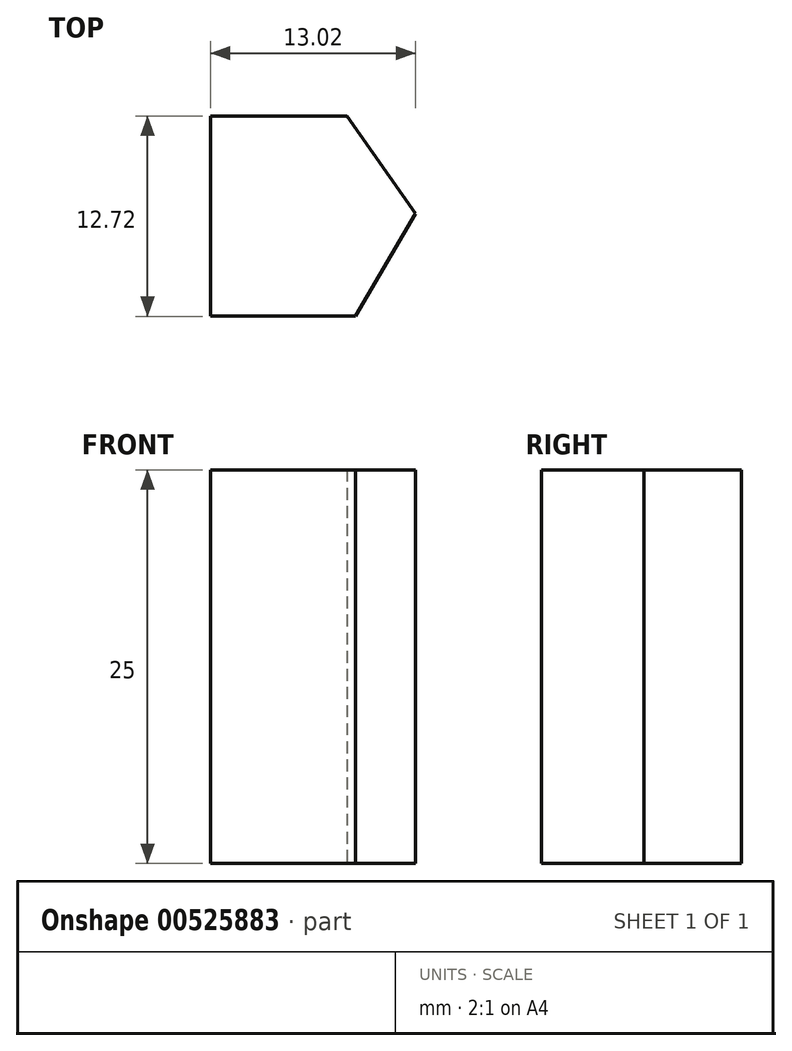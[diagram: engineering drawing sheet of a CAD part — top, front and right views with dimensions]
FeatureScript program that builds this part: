
annotation { "Feature Type Name" : "Feature", "Feature Type Description" : "" }
export const myFeature = defineFeature(function(context is Context, id is Id, definition is map)
    precondition{}
    {
        {
            var Q0;
            Q0=qCreatedBy(makeId("Top.planeOp"),FACE);
            var sketch = newSketch(context, id + "F0", { "sketchPlane" : qUnion([Q0])});
            skLineSegment(sketch, "E0", {"start": v(-57.05, 52.09) * mm, "end": v(-57.05, 26.66) * mm});
            skLineSegment(sketch, "E1", {"start": v(-68.83, 52.09) * mm, "end": v(-44.03, 52.09) * mm});
            skLineSegment(sketch, "E2", {"start": v(-30.38, 52.09) * mm, "end": v(-23.56, 41.55) * mm});
            skLineSegment(sketch, "E3", {"start": v(-17.98, 52.09) * mm, "end": v(-32.86, 26.66) * mm});
            skLineSegment(sketch, "E4", {"start": v(-9.3, 52.09) * mm, "end": v(-9.3, 26.66) * mm});
            skLineSegment(sketch, "E5", {"start": v(-9.3, 26.66) * mm, "end": v(4.96, 26.66) * mm});
            skLineSegment(sketch, "E6", {"start": v(16.74, 52.09) * mm, "end": v(16.74, 26.66) * mm});
            skLineSegment(sketch, "E7", {"start": v(16.74, 26.66) * mm, "end": v(27.28, 26.66) * mm});
            skLineSegment(sketch, "E8", {"start": v(16.74, 39.37) * mm, "end": v(27.28, 39.37) * mm});
            skLineSegment(sketch, "E9", {"start": v(16.74, 52.09) * mm, "end": v(27.28, 52.09) * mm});
            skLineSegment(sketch, "E10", {"start": v(40.93, 26.66) * mm, "end": v(40.93, 52.09) * mm});
            skLineSegment(sketch, "E11", {"start": v(40.93, 52.09) * mm, "end": v(49.6, 52.09) * mm});
            skLineSegment(sketch, "E12", {"start": v(49.6, 52.09) * mm, "end": v(53.95, 45.89) * mm});
            skLineSegment(sketch, "E13", {"start": v(53.95, 45.89) * mm, "end": v(50.14, 39.37) * mm});
            skLineSegment(sketch, "E14", {"start": v(50.14, 39.37) * mm, "end": v(40.93, 39.37) * mm});
            skLineSegment(sketch, "E15", {"start": v(40.93, 39.37) * mm, "end": v(53.95, 26.66) * mm});
            skSolve(sketch);
        }
        {
            var Q0;
            Q0 = qSketchRegion(id + "F0", true);
            extrude(context, id + "F1", {"entities" : qUnion([Q0]), "depth" : 25 * mm, "offsetDistance" : 25 * mm});
        }
        {
            var Q0;
            Q0 = qSketchRegion(id + "F0", true);
            extrude(context, id + "F2", {"entities" : qUnion([Q0]), "operationType" : NewBodyOperationType.ADD, "depth" : 25 * mm, "offsetDistance" : 25 * mm});
        }
    });
